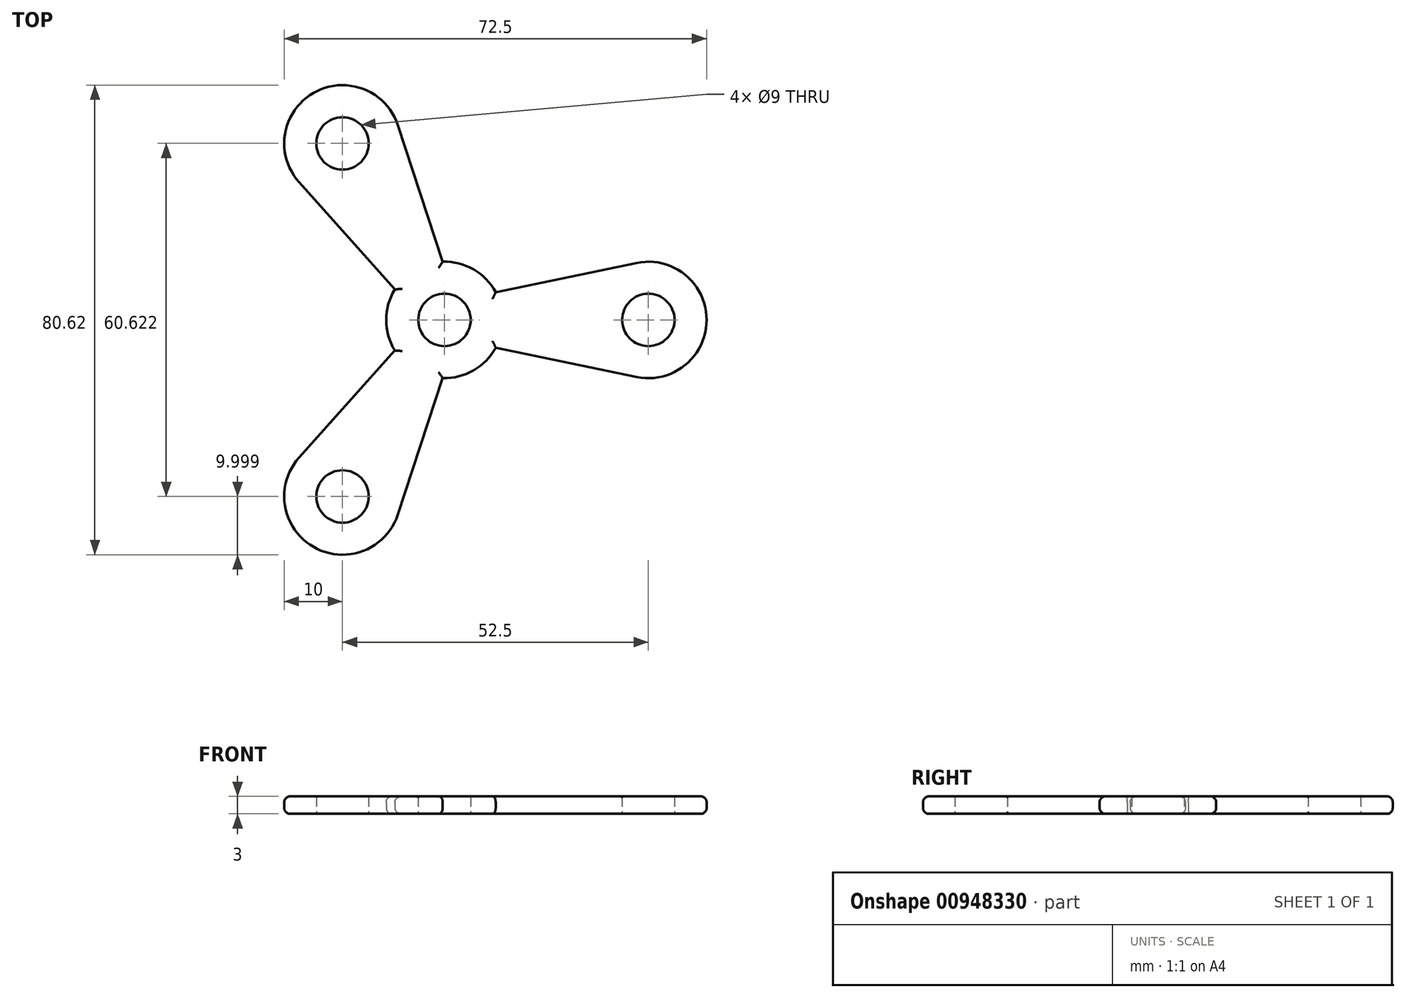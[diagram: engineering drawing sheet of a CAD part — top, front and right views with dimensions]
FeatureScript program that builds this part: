
annotation { "Feature Type Name" : "Feature", "Feature Type Description" : "" }
export const myFeature = defineFeature(function(context is Context, id is Id, definition is map)
    precondition{}
    {
        {
            var Q0;
            Q0=qCreatedBy(makeId("Top.planeOp"),FACE);
            var sketch = newSketch(context, id + "F0", { "sketchPlane" : qUnion([Q0])});
            skCircle(sketch, "E0", {"center": v(0, 0) * mm, "radius": 4.5 * mm});
            skCircle(sketch, "E1", {"center": v(35, 0) * mm, "radius": 4.5 * mm});
            skCircle(sketch, "E2.1.0", {"center": v(-17.5, 30.31) * mm, "radius": 4.5 * mm});
            skCircle(sketch, "E2.2.0", {"center": v(-17.5, -30.31) * mm, "radius": 4.5 * mm});
            skArc(sketch, "E3", {"start": v(8.8, 4.75) * mm, "mid": v(5, 8.66) * mm, "end": v(-0.29, 10) * mm});
            skArc(sketch, "E4", {"start": v(32.96, -9.79) * mm, "mid": v(45, 0) * mm, "end": v(32.96, 9.79) * mm});
            skLineSegment(sketch, "E5", {"start": v(8.8, 4.75) * mm, "end": v(32.96, 9.79) * mm});
            skLineSegment(sketch, "E6", {"start": v(8.8, -4.75) * mm, "end": v(32.96, -9.79) * mm});
            skArc(sketch, "E7.1.0", {"start": v(-8, 33.44) * mm, "mid": v(-22.5, 38.97) * mm, "end": v(-24.96, 23.65) * mm});
            skLineSegment(sketch, "E7.1.1", {"start": v(-8.51, 5.25) * mm, "end": v(-24.96, 23.65) * mm});
            skLineSegment(sketch, "E7.1.2", {"start": v(-0.29, 10) * mm, "end": v(-8, 33.44) * mm});
            skArc(sketch, "E7.2.0", {"start": v(-24.96, -23.65) * mm, "mid": v(-22.5, -38.97) * mm, "end": v(-8, -33.44) * mm});
            skLineSegment(sketch, "E7.2.1", {"start": v(-0.29, -10) * mm, "end": v(-8, -33.44) * mm});
            skLineSegment(sketch, "E7.2.2", {"start": v(-8.51, -5.25) * mm, "end": v(-24.96, -23.65) * mm});
            skArc(sketch, "E8.trimOffspring", {"start": v(-8.51, 5.25) * mm, "mid": v(-10, 0) * mm, "end": v(-8.51, -5.25) * mm});
            skArc(sketch, "E9.trimOffspring", {"start": v(-0.29, -10) * mm, "mid": v(5, -8.66) * mm, "end": v(8.8, -4.75) * mm});
            skSolve(sketch);
        }
        {
            var Q0;
            Q0=makeQuery(id+"F0.imprint","IMPRINT",FACE,{"disambiguationData":[TD([[makeQuery(id+"F0.imprint","IMPRINT",EDGE,{"derivedFrom":sQuery(id+"F0.wireOp",EDGE,"E0")}),-1.0]])]});
            extrude(context, id + "F1", {"entities" : qUnion([Q0]), "depth" : 3 * mm, "offsetDistance" : 25 * mm});
        }
        {
            var Q0;
            Q0=makeQuery(id+"F1.opExtrude","CAP_EDGE",EDGE,{"disambiguationData":[OSD([sQuery(id+"F0.wireOp",EDGE,"E6")])],"isStart":true});
            fillet(context, id + "F2", {"entities" : qUnion([Q0]), "radius" : 1 * mm, "tangentPropagation" : true, "allowEdgeOverflow" : false});
        }
        {
            var Q0;
            Q0=makeQuery(id+"F1.opExtrude","CAP_EDGE",EDGE,{"disambiguationData":[OSD([sQuery(id+"F0.wireOp",EDGE,"E9.trimOffspring")])],"isStart":true});
            var Q1;
            Q1=makeQuery(id+"F1.opExtrude","CAP_EDGE",EDGE,{"disambiguationData":[OSD([sQuery(id+"F0.wireOp",EDGE,"E6")])],"isStart":false});
            var Q2;
            Q2=makeQuery(id+"F1.opExtrude","CAP_EDGE",EDGE,{"disambiguationData":[OSD([sQuery(id+"F0.wireOp",EDGE,"E4")])],"isStart":false});
            var Q3;
            Q3=makeQuery(id+"F1.opExtrude","CAP_EDGE",EDGE,{"disambiguationData":[OSD([sQuery(id+"F0.wireOp",EDGE,"E5")])],"isStart":false});
            var Q4;
            Q4=makeQuery(id+"F1.opExtrude","CAP_EDGE",EDGE,{"disambiguationData":[OSD([sQuery(id+"F0.wireOp",EDGE,"E7.1.1")])],"isStart":false});
            var Q5;
            Q5=makeQuery(id+"F1.opExtrude","CAP_EDGE",EDGE,{"disambiguationData":[OSD([sQuery(id+"F0.wireOp",EDGE,"E7.1.2")])],"isStart":false});
            var Q6;
            Q6=makeQuery(id+"F1.opExtrude","CAP_EDGE",EDGE,{"disambiguationData":[OSD([sQuery(id+"F0.wireOp",EDGE,"E7.2.2")])],"isStart":false});
            var Q7;
            Q7=makeQuery(id+"F1.opExtrude","CAP_EDGE",EDGE,{"disambiguationData":[OSD([sQuery(id+"F0.wireOp",EDGE,"E8.trimOffspring")])],"isStart":false});
            var Q8;
            Q8=makeQuery(id+"F1.opExtrude","CAP_EDGE",EDGE,{"disambiguationData":[OSD([sQuery(id+"F0.wireOp",EDGE,"E7.1.2")])],"isStart":true});
            var Q9;
            Q9=makeQuery(id+"F1.opExtrude","CAP_EDGE",EDGE,{"disambiguationData":[OSD([sQuery(id+"F0.wireOp",EDGE,"E7.2.1")])],"isStart":true});
            var Q10;
            Q10=makeQuery(id+"F1.opExtrude","CAP_EDGE",EDGE,{"disambiguationData":[OSD([sQuery(id+"F0.wireOp",EDGE,"E7.2.1")])],"isStart":false});
            var Q11;
            Q11=makeQuery(id+"F1.opExtrude","CAP_EDGE",EDGE,{"disambiguationData":[OSD([sQuery(id+"F0.wireOp",EDGE,"E3")])],"isStart":false});
            var Q12;
            Q12=makeQuery(id+"F1.opExtrude","CAP_EDGE",EDGE,{"disambiguationData":[OSD([sQuery(id+"F0.wireOp",EDGE,"E9.trimOffspring")])],"isStart":false});
            fillet(context, id + "F3", {"entities" : qUnion([Q0, Q1, Q2, Q3, Q4, Q5, Q6, Q7, Q8, Q9, Q10, Q11, Q12]), "radius" : 1 * mm, "tangentPropagation" : true, "allowEdgeOverflow" : false});
        }
        {
            var Q0;
            Q0=makeQuery(id+"F1.opExtrude","CAP_EDGE",EDGE,{"disambiguationData":[OSD([sQuery(id+"F0.wireOp",EDGE,"E3")])],"isStart":true});
            fillet(context, id + "F4", {"entities" : qUnion([Q0]), "radius" : 1 * mm, "tangentPropagation" : true, "allowEdgeOverflow" : false});
        }
        {
            var Q0;
            Q0=makeQuery(id+"F1.opExtrude","CAP_EDGE",EDGE,{"disambiguationData":[OSD([sQuery(id+"F0.wireOp",EDGE,"E8.trimOffspring")])],"isStart":true});
            fillet(context, id + "F5", {"entities" : qUnion([Q0]), "radius" : 1 * mm, "tangentPropagation" : true, "allowEdgeOverflow" : false});
        }
        {
            var Q0;
            {var subQ0=sQuery(id+"F0.wireOp",EDGE,"E7.2.1");Q0=makeQuery(id+"F3.opFillet","BLEND_EDGE",EDGE,{"blendedFrom":[makeQuery(id+"F1.opExtrude","CAP_EDGE",EDGE,{"disambiguationData":[OSD([subQ0])],"isStart":false}),makeQuery(id+"F1.opExtrude","SWEPT_FACE",FACE,{"disambiguationData":[OSD([subQ0])]})],"blendedInto":[makeQuery(id+"F1.opExtrude","SWEPT_FACE",FACE,{"disambiguationData":[OSD([subQ0])]})]});}
            var Q1;
            Q1=makeQuery(id+"F1.opExtrude","CAP_EDGE",EDGE,{"disambiguationData":[OSD([sQuery(id+"F0.wireOp",EDGE,"E0")])],"isStart":false});
            fillet(context, id + "F6", {"entities" : qUnion([Q0, Q1]), "radius" : 0.25 * mm, "tangentPropagation" : true, "allowEdgeOverflow" : false});
        }
        {
            var Q0;
            Q0=makeQuery(id+"F1.opExtrude","CAP_EDGE",EDGE,{"disambiguationData":[OSD([sQuery(id+"F0.wireOp",EDGE,"E2.1.0")])],"isStart":false});
            fillet(context, id + "F7", {"entities" : qUnion([Q0]), "radius" : .25 * mm, "tangentPropagation" : true, "allowEdgeOverflow" : false});
        }
        {
            var Q0;
            Q0=makeQuery(id+"F1.opExtrude","CAP_EDGE",EDGE,{"disambiguationData":[OSD([sQuery(id+"F0.wireOp",EDGE,"E2.2.0")])],"isStart":false});
            fillet(context, id + "F8", {"entities" : qUnion([Q0]), "radius" : .25 * mm, "tangentPropagation" : true, "allowEdgeOverflow" : false});
        }
        {
            var Q0;
            Q0=makeQuery(id+"F1.opExtrude","CAP_EDGE",EDGE,{"disambiguationData":[OSD([sQuery(id+"F0.wireOp",EDGE,"E1")])],"isStart":false});
            var Q1;
            Q1=makeQuery(id+"F1.opExtrude","CAP_EDGE",EDGE,{"disambiguationData":[OSD([sQuery(id+"F0.wireOp",EDGE,"E1")])],"isStart":true});
            fillet(context, id + "F9", {"entities" : qUnion([Q0, Q1]), "radius" : 0.25 * mm, "tangentPropagation" : true, "allowEdgeOverflow" : false});
        }
        {
            var Q0;
            Q0=makeQuery(id+"F1.opExtrude","CAP_EDGE",EDGE,{"disambiguationData":[OSD([sQuery(id+"F0.wireOp",EDGE,"E2.1.0")])],"isStart":true});
            var Q1;
            {var subQ0=sQuery(id+"F0.wireOp",EDGE,"E2.1.0");Q1=makeQuery(id+"F7.opFillet","BLEND_EDGE",EDGE,{"blendedFrom":[makeQuery(id+"F1.opExtrude","CAP_EDGE",EDGE,{"disambiguationData":[OSD([subQ0])],"isStart":false}),makeQuery(id+"F1.opExtrude","SWEPT_FACE",FACE,{"disambiguationData":[OSD([subQ0])]})],"blendedInto":[makeQuery(id+"F1.opExtrude","SWEPT_FACE",FACE,{"disambiguationData":[OSD([subQ0])]})]});}
            fillet(context, id + "F10", {"entities" : qUnion([Q0, Q1]), "radius" : .25 * mm, "tangentPropagation" : true, "allowEdgeOverflow" : false});
        }
        {
            var Q0;
            Q0=makeQuery(id+"F1.opExtrude","CAP_EDGE",EDGE,{"disambiguationData":[OSD([sQuery(id+"F0.wireOp",EDGE,"E2.2.0")])],"isStart":true});
            fillet(context, id + "F11", {"entities" : qUnion([Q0]), "radius" : .25 * mm, "tangentPropagation" : true, "allowEdgeOverflow" : false});
        }
        {
            var Q0;
            Q0=makeQuery(id+"F1.opExtrude","CAP_EDGE",EDGE,{"disambiguationData":[OSD([sQuery(id+"F0.wireOp",EDGE,"E0")])],"isStart":true});
            fillet(context, id + "F12", {"entities" : qUnion([Q0]), "radius" : .25 * mm, "tangentPropagation" : true, "allowEdgeOverflow" : false});
        }
    });
